# Revit family: EKF_EE_КомплектПанелейЦоколяTrivia_AVERES
name_source: partatom
category: Электрооборудование
units: mm (PartAtom-declared; Revit-internal decimal feet)

## family parameters
Всегда вертикально = Нет
На основе рабочей плоскости = Да
Общий = Да
При загрузке вырезать с полостями = Нет
Размер круглого соединителя = Использовать диаметр
Тип детали = Силовой щит
Точка расчета площади = Нет

## types (8) — shared parameters
ADSK_Единица измерения = шт.
ADSK_Завод-изготовитель = EKF
ADSK_Количество = 1
ADSK_Марка = Комплект панелей цоколя
ADSK_Материал = RAL 7035_Сталь
ADSK_Обозначение = Комплект панелей цоколя
ADSK_Размер_Глубина = 16 мм
Изготовитель = EKF
Отметка по умолчанию = 1219.2 мм
Серия номенклатуры = Averes
Степень защиты IP = -
ТВ = EKF_2_TRIVIA_AVERES
Тип установки = -
zero-valued in all types: ADSK_Масса

## per-type parameters (varying)
| type | ADSK_Код изделия | ADSK_Наименование | ADSK_Размер_Высота | ADSK_Размер_Ширина | Тип |
| Комплект панелей  цоколя Ш300В200 EKF AVERES (2шт) | BPU3020 | Комплект панелей цоколя Ш300В200 EKF AVERES (2шт) | 200 мм | 278 мм | 486 мм |
| Комплект панелей цоколя Ш300В100 EKF AVERES (2 шт) | BP300W2 | Комплект панелей цоколя Ш300В100 EKF AVERES (2шт) | 100 мм | 278 мм | 487 мм |
| Комплект панелей цоколя Ш400В100 EKF AVERES (2шт) | BP400W2 | Комплект панелей цоколя Ш400В100 EKF AVERES (2шт) | 100 мм | 378 мм | 488 мм |
| Комплект панелей цоколя Ш400В200 EKF AVERES (2шт) | ВPU4020 | Комплект панелей цоколя Ш400В200 EKF AVERES (2шт) | 200 мм | 378 мм | 489 мм |
| Комплект панелей цоколя Ш600В100 EKF AVERES (2шт) | BP600W2 | Комплект панелей цоколя Ш600В100 EKF AVERES (2шт) | 100 мм | 578 мм | 490 мм |
| Комплект панелей цоколя Ш600В200 EKF AVERES (2 шт) | ВPU6020 | Комплект панелей цоколя Ш600В200 EKF AVERES (2шт) | 200 мм | 578 мм | 491 мм |
| Комплект панелей цоколя Ш800В100 EKF AVERES (2шт) | BP800W2 | Комплект панелей цоколя Ш800В100 EKF AVERES (2шт) | 100 мм | 778 мм | 492 мм |
| Комплект панелей цоколя Ш800В200 EKF AVERES (2 шт) | ВPU8020 | Комплект панелей цоколя Ш800В200 EKF AVERES (2шт) | 200 мм | 778 мм | 493 мм |
